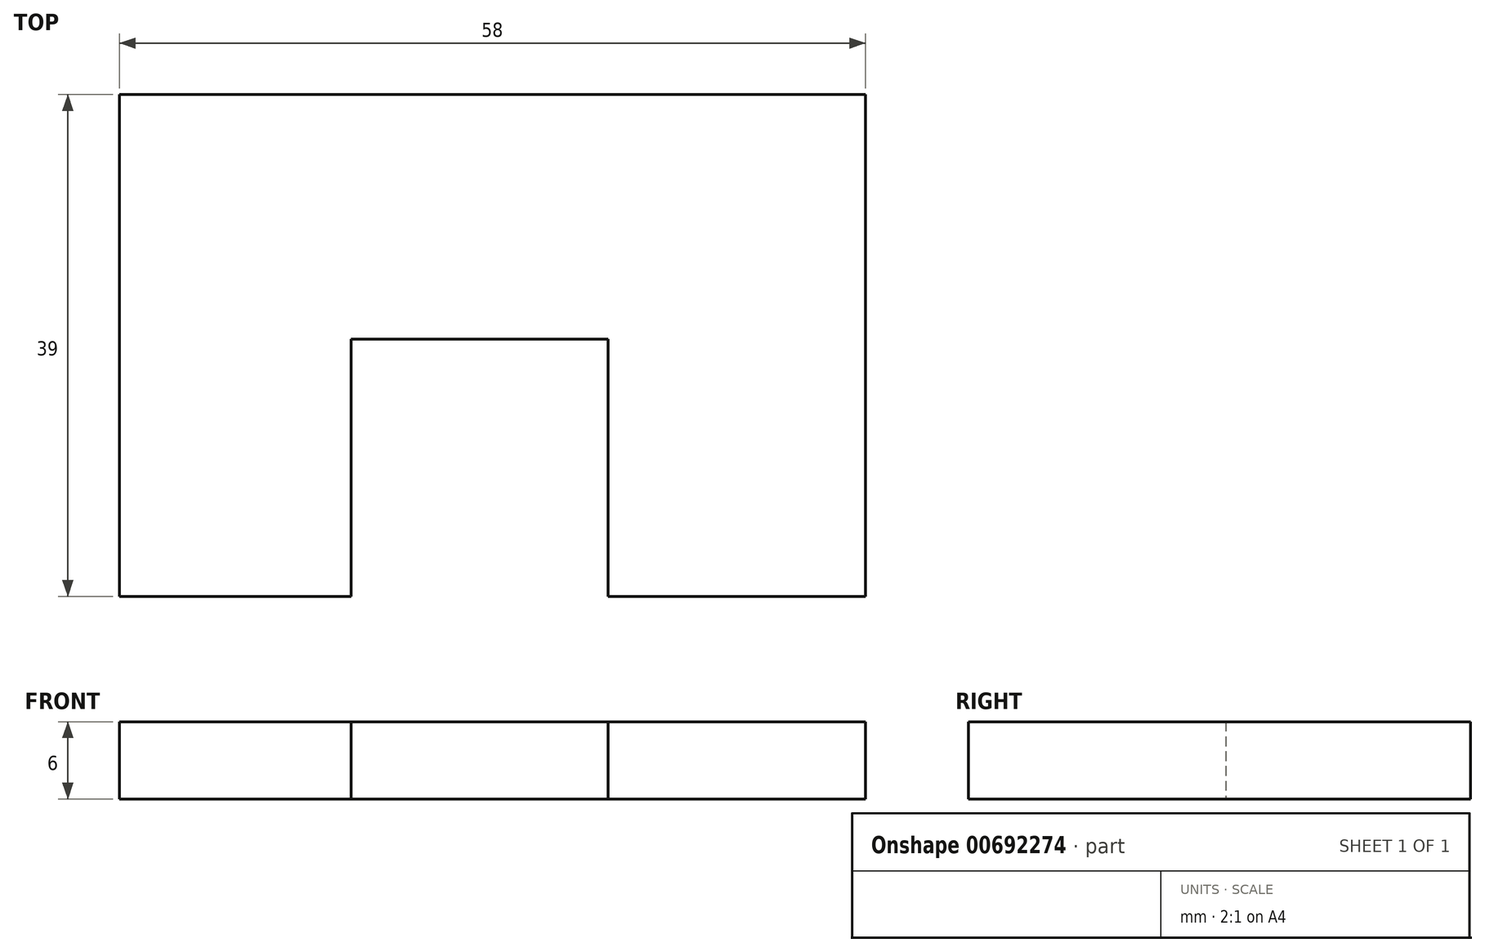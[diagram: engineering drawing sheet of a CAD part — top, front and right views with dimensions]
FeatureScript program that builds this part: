
annotation { "Feature Type Name" : "Feature", "Feature Type Description" : "" }
export const myFeature = defineFeature(function(context is Context, id is Id, definition is map)
    precondition{}
    {
        {
            var Q0;
            Q0=qCreatedBy(makeId("Top.planeOp"),FACE);
            var sketch = newSketch(context, id + "F0", { "sketchPlane" : qUnion([Q0])});
            skLineSegment(sketch, "E0", {"start": v(0, 0) * mm, "end": v(0, 39) * mm});
            skLineSegment(sketch, "E1", {"start": v(0, 39) * mm, "end": v(58, 39) * mm});
            skLineSegment(sketch, "E2", {"start": v(58, 39) * mm, "end": v(58, 0) * mm});
            skLineSegment(sketch, "E3", {"start": v(58, 0) * mm, "end": v(38, 0) * mm});
            skLineSegment(sketch, "E4", {"start": v(38, 0) * mm, "end": v(38, 20) * mm});
            skLineSegment(sketch, "E5", {"start": v(38, 20) * mm, "end": v(18, 20) * mm});
            skLineSegment(sketch, "E6", {"start": v(18, 20) * mm, "end": v(18, 0) * mm});
            skLineSegment(sketch, "E7", {"start": v(18, 0) * mm, "end": v(0, 0) * mm});
            skSolve(sketch);
        }
        {
            var Q0;
            Q0 = qSketchRegion(id + "F0", true);
            extrude(context, id + "F1", {"entities" : qUnion([Q0]), "depth" : 6 * mm, "offsetDistance" : 25.4 * mm});
        }
    });
